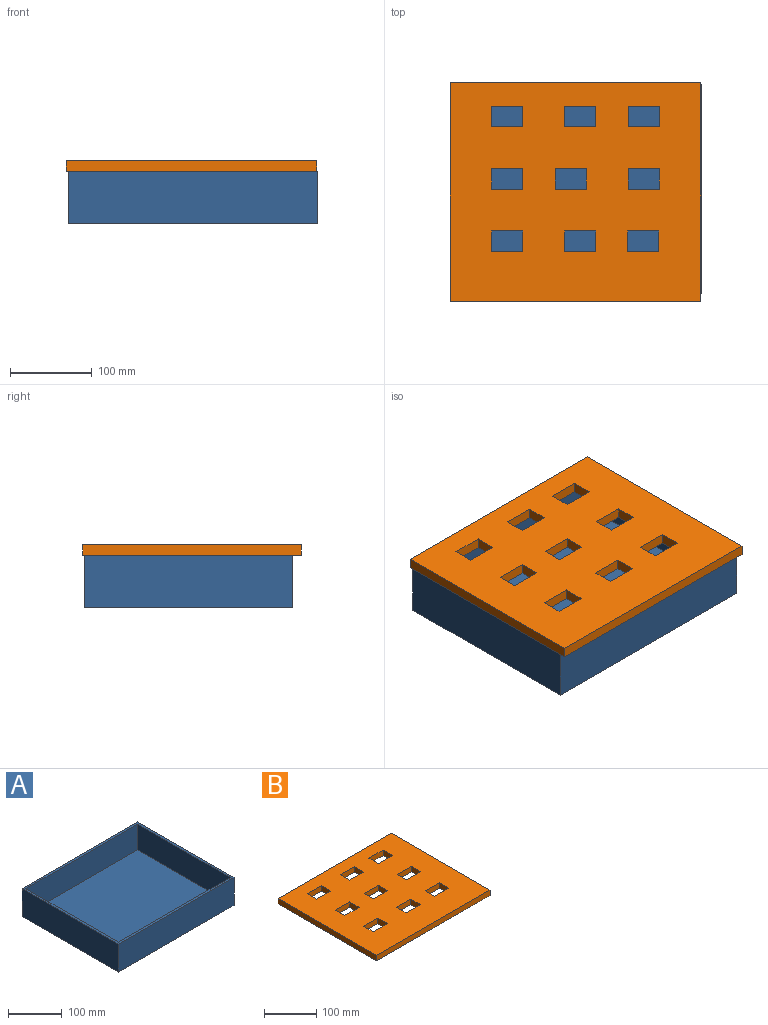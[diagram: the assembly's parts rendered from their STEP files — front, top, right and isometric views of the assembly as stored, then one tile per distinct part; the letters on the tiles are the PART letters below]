
ASSEMBLY  parts=2 mates=1
PART A: 11 faces, bbox 304.8x254x63.5 mm
  f0: plane 304.8x254mm, normal (0,0,1), area 5574.2mm2, adj f1,f2,f3,f4,f6,f7,f8,f9
  f1: plane 304.8x63.5mm, normal (0,1,0), area 19354.8mm2, adj f0,f2,f4,f5
  f2: plane 254x63.5mm, normal (-1,0,0), area 16129mm2, adj f0,f1,f3,f5
  f3: plane 304.8x63.5mm, normal (0,-1,0), area 19354.8mm2, adj f0,f2,f4,f5
  f4: plane 254x63.5mm, normal (1,0,0), area 16129mm2, adj f0,f1,f3,f5
  f5: plane 304.8x254mm, normal (0,0,-1), area 77419.2mm2, adj f1,f2,f3,f4
  f6: plane 294.64x58.42mm, normal (0,-1,0), area 17212.9mm2, adj f0,f7,f9,f10
  f7: plane 243.84x58.42mm, normal (1,0,0), area 14245.1mm2, adj f0,f6,f8,f10
  f8: plane 294.64x58.42mm, normal (0,1,0), area 17212.9mm2, adj f0,f7,f9,f10
  f9: plane 243.84x58.42mm, normal (-1,0,0), area 14245.1mm2, adj f0,f6,f8,f10
  f10: plane 294.64x243.84mm, normal (0,0,1), area 71845mm2, adj f6,f7,f8,f9
PART B: 92 faces, bbox 306.1x266.7x12.7 mm
  f0: plane 43.18x30.48mm, normal (0,0,-1), area 348.4mm2, adj f33,f34,f35,f46,f75,f76,f77,f88
  f1: plane 43.18x30.48mm, normal (0,0,-1), area 348.4mm2, adj f30,f31,f32,f45,f72,f73,f74,f87
  f2: plane 43.18x30.48mm, normal (0,0,-1), area 348.4mm2, adj f27,f28,f29,f44,f69,f70,f71,f86
  f3: plane 43.18x30.48mm, normal (0,0,-1), area 348.4mm2, adj f24,f25,f26,f43,f66,f67,f68,f85
  f4: plane 43.18x30.48mm, normal (0,0,-1), area 348.4mm2, adj f21,f22,f23,f42,f63,f64,f65,f84
  f5: plane 43.18x30.48mm, normal (0,0,-1), area 348.4mm2, adj f18,f19,f20,f41,f60,f61,f62,f83
  f6: plane 43.18x30.48mm, normal (0,0,-1), area 348.4mm2, adj f15,f16,f17,f40,f57,f58,f59,f82
  f7: plane 43.18x30.48mm, normal (0,0,-1), area 348.4mm2, adj f12,f13,f14,f39,f54,f55,f56,f81
  f8: plane 43.18x30.48mm, normal (0,0,-1), area 348.4mm2, adj f36,f37,f38,f47,f78,f79,f80,f89
  f9: plane 306.07x12.7mm, normal (0,-1,0), area 3887.1mm2, adj f10,f48,f49,f50
  f10: plane 266.7x12.7mm, normal (1,0,0), area 3387.1mm2, adj f9,f11,f49,f50
  f11: plane 306.07x12.7mm, normal (0,1,0), area 3887.1mm2, adj f10,f48,f49,f50
  f12: plane 25.4x12.7mm, normal (1,0,0), area 322.6mm2, adj f7,f13,f39,f50
  f13: plane 38.1x12.7mm, normal (0,-1,0), area 483.9mm2, adj f7,f12,f14,f50
  f14: plane 25.4x12.7mm, normal (-1,0,0), area 322.6mm2, adj f7,f13,f39,f50
  f15: plane 25.4x12.7mm, normal (1,0,0), area 322.6mm2, adj f6,f16,f40,f50
  f16: plane 38.1x12.7mm, normal (0,-1,0), area 483.9mm2, adj f6,f15,f17,f50
  f17: plane 25.4x12.7mm, normal (-1,0,0), area 322.6mm2, adj f6,f16,f40,f50
  f18: plane 25.4x12.7mm, normal (1,0,0), area 322.6mm2, adj f5,f19,f41,f50
  f19: plane 38.1x12.7mm, normal (0,-1,0), area 483.9mm2, adj f5,f18,f20,f50
  f20: plane 25.4x12.7mm, normal (-1,0,0), area 322.6mm2, adj f5,f19,f41,f50
  f21: plane 38.1x12.7mm, normal (0,1,0), area 483.9mm2, adj f4,f22,f42,f50
  f22: plane 25.4x12.7mm, normal (1,0,0), area 322.6mm2, adj f4,f21,f23,f50
  f23: plane 38.1x12.7mm, normal (0,-1,0), area 483.9mm2, adj f4,f22,f42,f50
  f24: plane 25.4x12.7mm, normal (1,0,0), area 322.6mm2, adj f3,f25,f43,f50
  f25: plane 38.1x12.7mm, normal (0,-1,0), area 483.9mm2, adj f3,f24,f26,f50
  f26: plane 25.4x12.7mm, normal (-1,0,0), area 322.6mm2, adj f3,f25,f43,f50
  f27: plane 25.4x12.7mm, normal (1,0,0), area 322.6mm2, adj f2,f28,f44,f50
  f28: plane 38.1x12.7mm, normal (0,-1,0), area 483.9mm2, adj f2,f27,f29,f50
  f29: plane 25.4x12.7mm, normal (-1,0,0), area 322.6mm2, adj f2,f28,f44,f50
  f30: plane 25.4x12.7mm, normal (1,0,0), area 322.6mm2, adj f1,f31,f45,f50
  f31: plane 38.1x12.7mm, normal (0,-1,0), area 483.9mm2, adj f1,f30,f32,f50
  f32: plane 25.4x12.7mm, normal (-1,0,0), area 322.6mm2, adj f1,f31,f45,f50
  f33: plane 25.4x12.7mm, normal (1,0,0), area 322.6mm2, adj f0,f34,f46,f50
  f34: plane 38.1x12.7mm, normal (0,-1,0), area 483.9mm2, adj f0,f33,f35,f50
  f35: plane 25.4x12.7mm, normal (-1,0,0), area 322.6mm2, adj f0,f34,f46,f50
  f36: plane 38.1x12.7mm, normal (0,-1,0), area 483.9mm2, adj f8,f37,f47,f50
  f37: plane 25.4x12.7mm, normal (-1,0,0), area 322.6mm2, adj f8,f36,f38,f50
  f38: plane 38.1x12.7mm, normal (0,1,0), area 483.9mm2, adj f8,f37,f47,f50
  f39: plane 38.1x12.7mm, normal (0,1,0), area 483.9mm2, adj f7,f12,f14,f50
  f40: plane 38.1x12.7mm, normal (0,1,0), area 483.9mm2, adj f6,f15,f17,f50
  f41: plane 38.1x12.7mm, normal (0,1,0), area 483.9mm2, adj f5,f18,f20,f50
  f42: plane 25.4x12.7mm, normal (-1,0,0), area 322.6mm2, adj f4,f21,f23,f50
  f43: plane 38.1x12.7mm, normal (0,1,0), area 483.9mm2, adj f3,f24,f26,f50
  f44: plane 38.1x12.7mm, normal (0,1,0), area 483.9mm2, adj f2,f27,f29,f50
  f45: plane 38.1x12.7mm, normal (0,1,0), area 483.9mm2, adj f1,f30,f32,f50
  f46: plane 38.1x12.7mm, normal (0,1,0), area 483.9mm2, adj f0,f33,f35,f50
  f47: plane 25.4x12.7mm, normal (1,0,0), area 322.6mm2, adj f8,f36,f38,f50
  f48: plane 266.7x12.7mm, normal (-1,0,0), area 3387.1mm2, adj f9,f11,f49,f50
  f49: plane 306.07x266.7mm, normal (0,0,-1), area 2883.9mm2, adj f9,f10,f11,f48,f51,f52,f53,f90
  f50: plane 306.07x266.7mm, normal (0,0,1), area 72919.2mm2, adj f9,f10,f11,f12,f13,f14,f15,f16
  f51: plane 300.99x10.16mm, normal (0,1,0), area 3058.1mm2, adj f49,f52,f90,f91
  f52: plane 261.62x10.16mm, normal (-1,0,0), area 2658.1mm2, adj f49,f51,f53,f91
  f53: plane 300.99x10.16mm, normal (0,-1,0), area 3058.1mm2, adj f49,f52,f90,f91
  f54: plane 30.48x10.16mm, normal (-1,0,0), area 309.7mm2, adj f7,f55,f81,f91
  f55: plane 43.18x10.16mm, normal (0,1,0), area 438.7mm2, adj f7,f54,f56,f91
  f56: plane 30.48x10.16mm, normal (1,0,0), area 309.7mm2, adj f7,f55,f81,f91
  f57: plane 30.48x10.16mm, normal (-1,0,0), area 309.7mm2, adj f6,f58,f82,f91
  f58: plane 43.18x10.16mm, normal (0,1,0), area 438.7mm2, adj f6,f57,f59,f91
  f59: plane 30.48x10.16mm, normal (1,0,0), area 309.7mm2, adj f6,f58,f82,f91
  f60: plane 30.48x10.16mm, normal (-1,0,0), area 309.7mm2, adj f5,f61,f83,f91
  f61: plane 43.18x10.16mm, normal (0,1,0), area 438.7mm2, adj f5,f60,f62,f91
  f62: plane 30.48x10.16mm, normal (1,0,0), area 309.7mm2, adj f5,f61,f83,f91
  f63: plane 43.18x10.16mm, normal (0,-1,0), area 438.7mm2, adj f4,f64,f84,f91
  f64: plane 30.48x10.16mm, normal (-1,0,0), area 309.7mm2, adj f4,f63,f65,f91
  f65: plane 43.18x10.16mm, normal (0,1,0), area 438.7mm2, adj f4,f64,f84,f91
  f66: plane 30.48x10.16mm, normal (-1,0,0), area 309.7mm2, adj f3,f67,f85,f91
  f67: plane 43.18x10.16mm, normal (0,1,0), area 438.7mm2, adj f3,f66,f68,f91
  f68: plane 30.48x10.16mm, normal (1,0,0), area 309.7mm2, adj f3,f67,f85,f91
  f69: plane 30.48x10.16mm, normal (-1,0,0), area 309.7mm2, adj f2,f70,f86,f91
  f70: plane 43.18x10.16mm, normal (0,1,0), area 438.7mm2, adj f2,f69,f71,f91
  f71: plane 30.48x10.16mm, normal (1,0,0), area 309.7mm2, adj f2,f70,f86,f91
  f72: plane 30.48x10.16mm, normal (-1,0,0), area 309.7mm2, adj f1,f73,f87,f91
  f73: plane 43.18x10.16mm, normal (0,1,0), area 438.7mm2, adj f1,f72,f74,f91
  f74: plane 30.48x10.16mm, normal (1,0,0), area 309.7mm2, adj f1,f73,f87,f91
  f75: plane 30.48x10.16mm, normal (-1,0,0), area 309.7mm2, adj f0,f76,f88,f91
  f76: plane 43.18x10.16mm, normal (0,1,0), area 438.7mm2, adj f0,f75,f77,f91
  f77: plane 30.48x10.16mm, normal (1,0,0), area 309.7mm2, adj f0,f76,f88,f91
  f78: plane 43.18x10.16mm, normal (0,1,0), area 438.7mm2, adj f8,f79,f89,f91
  f79: plane 30.48x10.16mm, normal (1,0,0), area 309.7mm2, adj f8,f78,f80,f91
  f80: plane 43.18x10.16mm, normal (0,-1,0), area 438.7mm2, adj f8,f79,f89,f91
  f81: plane 43.18x10.16mm, normal (0,-1,0), area 438.7mm2, adj f7,f54,f56,f91
  f82: plane 43.18x10.16mm, normal (0,-1,0), area 438.7mm2, adj f6,f57,f59,f91
  f83: plane 43.18x10.16mm, normal (0,-1,0), area 438.7mm2, adj f5,f60,f62,f91
  f84: plane 30.48x10.16mm, normal (1,0,0), area 309.7mm2, adj f4,f63,f65,f91
  f85: plane 43.18x10.16mm, normal (0,-1,0), area 438.7mm2, adj f3,f66,f68,f91
  f86: plane 43.18x10.16mm, normal (0,-1,0), area 438.7mm2, adj f2,f69,f71,f91
  f87: plane 43.18x10.16mm, normal (0,-1,0), area 438.7mm2, adj f1,f72,f74,f91
  f88: plane 43.18x10.16mm, normal (0,-1,0), area 438.7mm2, adj f0,f75,f77,f91
  f89: plane 30.48x10.16mm, normal (-1,0,0), area 309.7mm2, adj f8,f78,f80,f91
  f90: plane 261.62x10.16mm, normal (1,0,0), area 2658.1mm2, adj f49,f51,f53,f91
  f91: plane 300.99x261.62mm, normal (0,0,-1), area 66899.9mm2, adj f51,f52,f53,f54,f55,f56,f57,f58
PLACE A t=(-2.24,-23.88,3.31)mm
PLACE B t=(147.62,-34.04,79.51)mm
MATE fastened B.f49 <-> A.f0  axis (0,0,1) through (-155.35,121.54,66.81)mm
